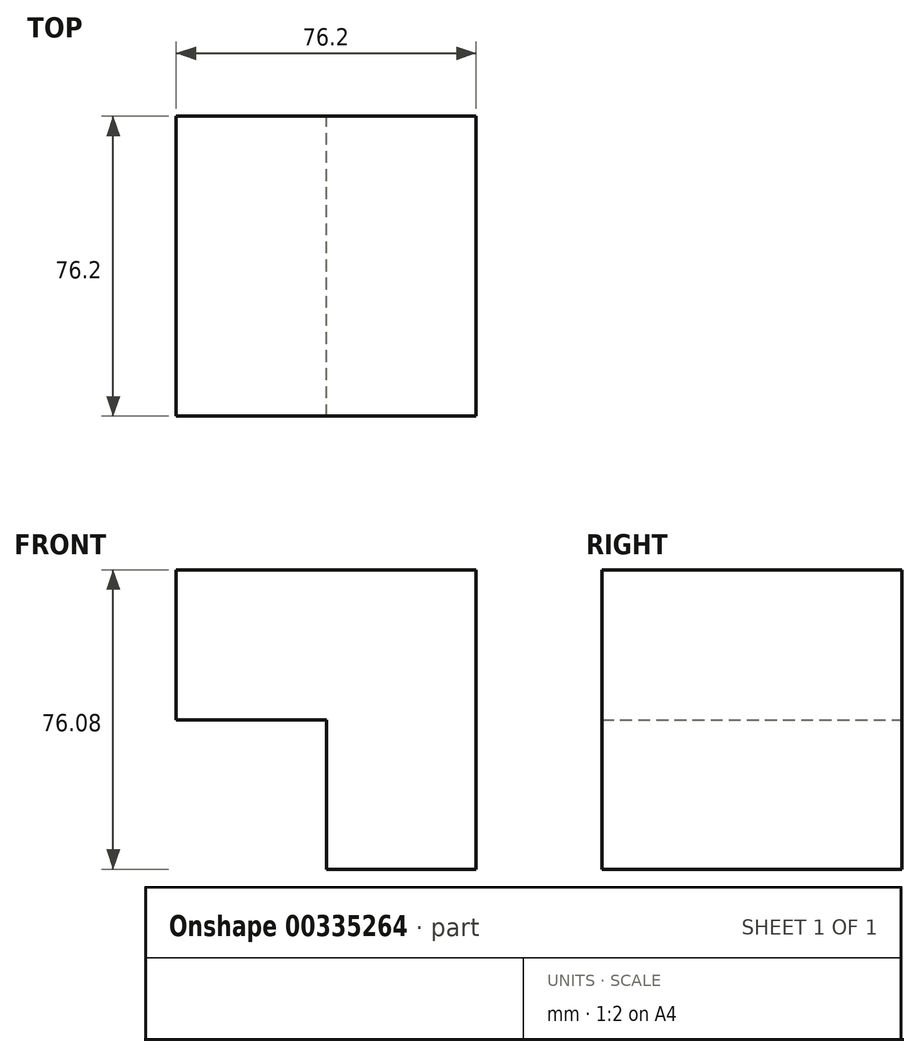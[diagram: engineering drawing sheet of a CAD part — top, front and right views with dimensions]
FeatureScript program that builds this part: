
annotation { "Feature Type Name" : "Feature", "Feature Type Description" : "" }
export const myFeature = defineFeature(function(context is Context, id is Id, definition is map)
    precondition{}
    {
        {
            var Q0;
            Q0=qCreatedBy(makeId("Front.planeOp"),FACE);
            var sketch = newSketch(context, id + "F0", { "sketchPlane" : qUnion([Q0])});
            skLineSegment(sketch, "E0.bottom", {"start": v(-38.25, 38.13) * mm, "end": v(37.95, 38.13) * mm});
            skLineSegment(sketch, "E0.top", {"start": v(-38.25, 0) * mm, "end": v(37.95, 0) * mm});
            skLineSegment(sketch, "E0.left", {"start": v(-38.25, 38.13) * mm, "end": v(-38.25, 0) * mm});
            skLineSegment(sketch, "E0.right", {"start": v(37.95, 38.13) * mm, "end": v(37.95, 0) * mm});
            skLineSegment(sketch, "E1.bottom", {"start": v(37.95, -37.95) * mm, "end": v(0, -37.95) * mm});
            skLineSegment(sketch, "E1.top", {"start": v(37.95, 0) * mm, "end": v(0, 0) * mm});
            skLineSegment(sketch, "E1.left", {"start": v(37.95, -37.95) * mm, "end": v(37.95, 0) * mm});
            skLineSegment(sketch, "E1.right", {"start": v(0, -37.95) * mm, "end": v(0, 0) * mm});
            skSolve(sketch);
        }
        {
            var Q0;
            Q0 = qSketchRegion(id + "F0", true);
            extrude(context, id + "F1", {"entities" : qUnion([Q0]), "depth" : 76.2 * mm});
        }
    });
